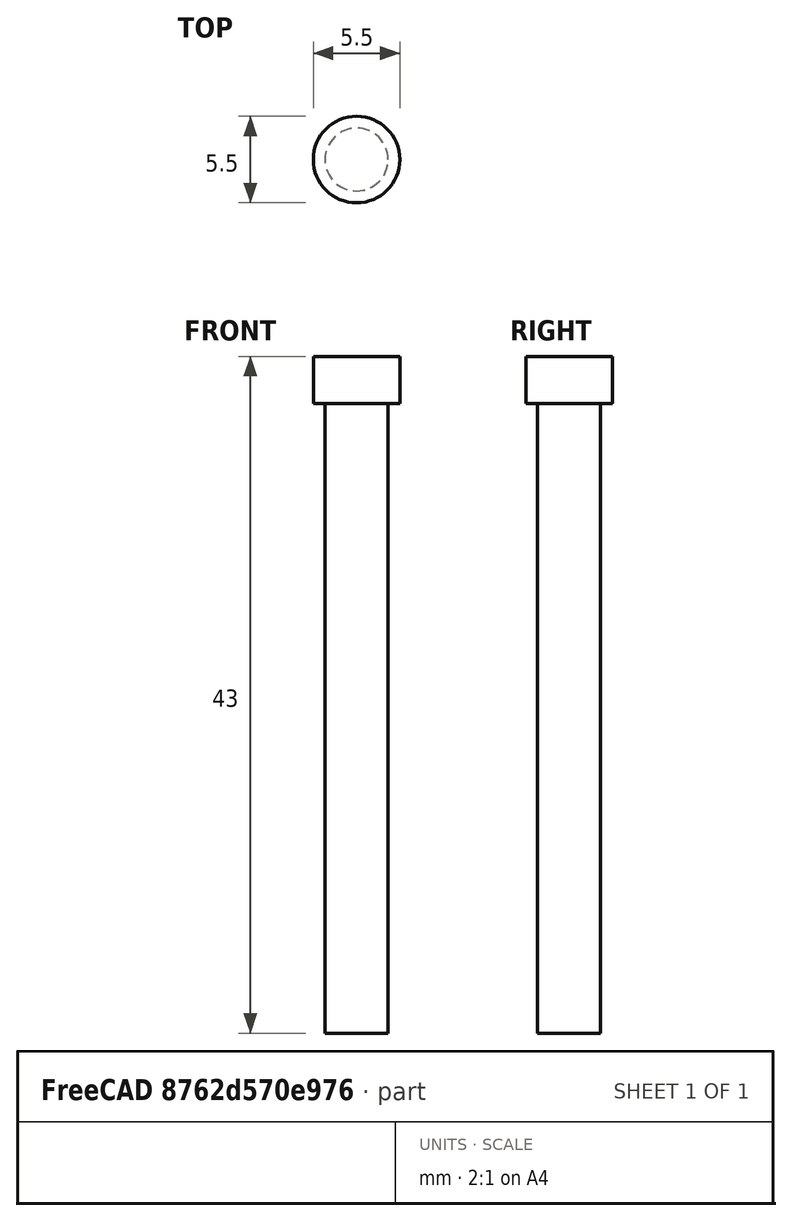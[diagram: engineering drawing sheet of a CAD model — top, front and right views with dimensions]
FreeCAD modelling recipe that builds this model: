
FCSTD DOCUMENT  (FreeCAD 0.18R14555 (Git shallow))
Label: m4-40
License: All rights reserved
LicenseURL: http://en.wikipedia.org/wiki/All_rights_reserved
objects: Sketcher::SketchObject×1, PartDesign::Revolution×1, PartDesign::Body×1
note: 4 computed .brp shape members not serialized (recipe doc carries the construction recipe); baked Part::Feature solids carry a one-line shape summary decoded from their .brp

FEATURE [Sketcher::SketchObject] Sketch
  MapMode = 5
  Placement = pos=(0,0,0) rot=(1,0,0;1.5708rad)
  Support = -> [XZ_Plane]
  sketch-geometry (6):
    g0: LineSegment StartX=0 StartY=0 StartZ=0 EndX=0 EndY=43 EndZ=0
    g1: LineSegment StartX=0 StartY=43 StartZ=0 EndX=2.75 EndY=43 EndZ=0
    g2: LineSegment StartX=2.75 StartY=43 StartZ=0 EndX=2.75 EndY=40 EndZ=0
    g3: LineSegment StartX=2.75 StartY=40 StartZ=0 EndX=2 EndY=40 EndZ=0
    g4: LineSegment StartX=2 StartY=40 StartZ=0 EndX=2 EndY=0 EndZ=0
    g5: LineSegment StartX=2 StartY=0 StartZ=0 EndX=0 EndY=0 EndZ=0
  constraints (17):
    c: Vertical(g0)
    c: Coincident(g0,g1)
    c: Horizontal(g1)
    c: Coincident(g1,g2)
    c: Vertical(g2)
    c: Coincident(g2,g3)
    c: Horizontal(g3)
    c: Coincident(g3,g4)
    c: Vertical(g4)
    c: Coincident(g4,g5)
    c: Coincident(g5,g0)
    c: Horizontal(g5)
    c: Coincident(g0,g-1)
    c: DistanceX(g5,g5) = 2
    c: DistanceY(g4,g4) = 40
    c: DistanceX(g1,g1) = 2.75
    c: DistanceY(g2,g2) = 3
FEATURE [PartDesign::Revolution] Revolution
  Angle = 360
  Axis = (0,-2e-16,1)
  Base = (0,0,0)
  Placement = pos=(0,0,0) rot=(1,0,0;1.5708rad)
  Profile = -> Sketch
  ReferenceAxis = -> Sketch [V_Axis]
  Reversed = true
FEATURE [PartDesign::Body] Body
  Group = -> [Sketch,Revolution]
  Origin = -> Origin
  Tip = -> Revolution
